# Revit family: RET_TP_V2_RFA
name_source: partatom
category: Data Devices
units: mm (PartAtom-declared; Revit-internal decimal feet)

## family parameters
Cut with Voids When Loaded = No
Host = Face
Maintain Annotation Orientation = Yes
Part Type = Normal
Room Calculation Point = No
Round Connector Dimension = Use Diameter
Shared = No

## types (10) — shared parameters
Body Material = Danfoss Plastic White
Control Polution Situation = Degree 2
Default Elevation = 1500 mm  [stored 4.92126 ft]
Description = Room Thermostat
H1_2 = 39 mm  [stored 0.127953 ft]
H_2 = 43 mm  [stored 0.141076 ft]
IP Rating = IP30
IfcExportAs = IfcElectricApplianceType
L1_2 = 39 mm  [stored 0.127953 ft]
LOD 200 = No
LOD 350 = Yes
L_2 = 43 mm  [stored 0.141076 ft]
Manufacturer = Danfoss
Max Ambient Temperature = 40 °C
Min Temperature Setting = 5 °C
Operating Temperature Range = 0-40 °C
R1 = 33 mm  [stored 0.108268 ft]
R2 = 185 mm  [stored 0.606955 ft]
Rated Impulse Voltage = 4 kV
URL = https://store.danfoss.com
W3 = 1 mm  [stored 0.00328084 ft]

## per-type parameters (varying)
| type | Button_H | Fault Indication | IfcExportType | LCD backlight | Max Temperature Setting | Maximum Range | Model | Model Type | Operating Frequency | Output | Power Supply RT | RX1-S | Switch Rating | Switch Type | Voltage | W1 | W2 | W4 | W5 | W6 | Weight | Width |
| RET1001M_V2_087N6461 | -2 mm  [stored -0.00656168 ft] | - | RET1001 | - | 30 °C | - | 087N6461 | RET1001M_V2 | 50/60 Hz | Volt Free | 230 VAC | No | 3 A (1 A) at 230 VAC | 1 x SPDT Type 1B | 230 V | 6 mm  [stored 0.019685 ft] | 6 mm  [stored 0.019685 ft] | 4 mm  [stored 0.0131234 ft] | 2 mm  [stored 0.00656168 ft] | 17 mm  [stored 0.0557743 ft] | 0.13 kg | 30 mm  [stored 0.0984252 ft] |
| RET2001B_087N6471 | 1 mm  [stored 0.00328084 ft] | Yes | RET2001 | Yes | 35 °C | - | 087N6471 | RET2001B | - | Volt Free | 3 V DC Battery (2x AA Alkaline Batteries) | No | 3 A (1 A) at 230 VAC | 1 x SPDT Type 1B | 3 V | 2 mm  [stored 0.00656168 ft] | 7 mm  [stored 0.0229659 ft] | 6 mm  [stored 0.019685 ft] | 2 mm  [stored 0.00656168 ft] | 13 mm  [stored 0.0426509 ft] | 0.20 kg | 28 mm  [stored 0.0918635 ft] |
| RET2001RF + RX1-S_V2_087N6477 | 1 mm  [stored 0.00328084 ft] | Yes | RET2001 | Yes | 35 °C | 30 m | 087N6477 | RET2001RF + RX1-S_V2 | - | RF 433.92 Mhz | 3 V DC Battery (2x AA Alkaline Batteries) | Yes | 3 A (1 A) at 230 VAC (RX1-S V2) | 1 x SPDT Type 1B (RX1-S V2) | 230 V | 2 mm  [stored 0.00656168 ft] | 7 mm  [stored 0.0229659 ft] | 6 mm  [stored 0.019685 ft] | 2 mm  [stored 0.00656168 ft] | 13 mm  [stored 0.0426509 ft] | 0.40 kg | 28 mm  [stored 0.0918635 ft] |
| TP5001B_087N7931 | 1 mm  [stored 0.00328084 ft] | Yes | TP5001 | Yes | 35 °C | - | 087N7931 | TP5001B | - | Volt Free | 3 V DC Battery (2x AA Alkaline Batteries) | No | 3 A (1 A) at 230 VAC | 1 x SPDT Type 1B | 3 V | 2 mm  [stored 0.00656168 ft] | 7 mm  [stored 0.0229659 ft] | 6 mm  [stored 0.019685 ft] | 2 mm  [stored 0.00656168 ft] | 13 mm  [stored 0.0426509 ft] | 0.20 kg | 28 mm  [stored 0.0918635 ft] |
| TP5001RF_087N7933 | 1 mm  [stored 0.00328084 ft] | Yes | TP5001 | Yes | 35 °C | 30 m | 087N7933 | TP5001RF | - | RF 433.92 Mhz | 3 V DC Battery (2x AA Alkaline Batteries) | No | - | - | 3 V | 2 mm  [stored 0.00656168 ft] | 7 mm  [stored 0.0229659 ft] | 6 mm  [stored 0.019685 ft] | 2 mm  [stored 0.00656168 ft] | 13 mm  [stored 0.0426509 ft] | 0.20 kg | 28 mm  [stored 0.0918635 ft] |
| RET2001M_V2_087N6476 | 1 mm  [stored 0.00328084 ft] | Yes | RET2001 | Yes | 35 °C | - | 087N6476 | RET2001M_V2 | 50/60 Hz | Volt Free | 230 VAC | No | 3 A (1 A) at 230 VAC | 1 x SPDT Type 1B | 230 V | 2 mm  [stored 0.00656168 ft] | 6 mm  [stored 0.019685 ft] | 9 mm  [stored 0.0295276 ft] | 1 mm  [stored 0.00328084 ft] | 13 mm  [stored 0.0426509 ft] | 0.13 kg | 30 mm  [stored 0.0984252 ft] |
| TP5001M_V2_087N7935 | 1 mm  [stored 0.00328084 ft] | Yes | TP5001 | Yes | 35 °C | - | 087N7935 | TP5001M_V2 | 50/60 Hz | Volt Free | 230 VAC | No | 3 A (1 A) at 230 VAC | 1 x SPDT Type 1B | 230 V | 2 mm  [stored 0.00656168 ft] | 6 mm  [stored 0.019685 ft] | 9 mm  [stored 0.0295276 ft] | 1 mm  [stored 0.00328084 ft] | 13 mm  [stored 0.0426509 ft] | 0.20 kg | 30 mm  [stored 0.0984252 ft] |
| RET2001OT_V2_087N6478 | 1 mm  [stored 0.00328084 ft] | Yes | RET2001 | Yes | 35 °C | - | 087N6478 | RET2001OT_V2 | 50/60 Hz | Data 24 VDC Bus | 24 VDC power line from boiler | No | - | - | 24 V | 2 mm  [stored 0.00656168 ft] | 6 mm  [stored 0.019685 ft] | 9 mm  [stored 0.0295276 ft] | 1 mm  [stored 0.00328084 ft] | 13 mm  [stored 0.0426509 ft] | 0.18 kg | 30 mm  [stored 0.0984252 ft] |
| RET2001RF_087N6473 | 1 mm  [stored 0.00328084 ft] | Yes | RET2001 | Yes | 35 °C | 30 m | 087N6473 | RET2001RF | - | RF 433.92 Mhz | 3 V DC Battery (2x AA Alkaline Batteries) | No | - | - | 3 V | 2 mm  [stored 0.00656168 ft] | 7 mm  [stored 0.0229659 ft] | 6 mm  [stored 0.019685 ft] | 2 mm  [stored 0.00656168 ft] | 13 mm  [stored 0.0426509 ft] | 0.20 kg | 28 mm  [stored 0.0918635 ft] |
| TP5001RF + RX1-S_V2_087N7936 | 1 mm  [stored 0.00328084 ft] | Yes | TP5001 | Yes | 35 °C | 30 m | 087N7936 | TP5001RF + RX1-S_V2 | - | RF 433.92 Mhz | 3 V DC Battery (2x AA Alkaline Batteries) | Yes | 3 A (1 A) at 230 VAC (RX1-S V2) | 1 x SPDT Type 1B (RX1-S V2) | 230 V | 2 mm  [stored 0.00656168 ft] | 7 mm  [stored 0.0229659 ft] | 6 mm  [stored 0.019685 ft] | 2 mm  [stored 0.00656168 ft] | 13 mm  [stored 0.0426509 ft] | 0.46 kg | 28 mm  [stored 0.0918635 ft] |

note: [stored X ft] marks values corroborated as IEEE doubles in the binary element streams (Revit-internal decimal feet)

## geometry (parser evidence)
native form markers: Sweep x3
no freeform markers — native parametric forms only
